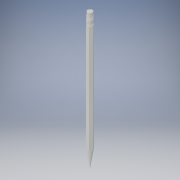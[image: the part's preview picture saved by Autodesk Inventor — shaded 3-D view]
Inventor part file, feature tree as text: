
AUTODESK INVENTOR PART (.ipt)
format: ipt  version: 2017 (Build 210142000, 142)  size: 200,192 bytes
history: native  units: in
note: dims shown in document units (in); Inventor stores cm internally (conversion verified against a paired STEP export)
features: sketch x5, other x4, extrude x2, revolve x1
ambient origin geometry x8: Origin, YZ Plane, XZ Plane, XY Plane, X Axis, Y Axis, Z Axis, Center Point
bodies: Body1 (feature_tree), Body2 (feature_tree)
feature tree (12):
  other  "pencil"
  extrude  "wooden part of pencil"  Depth=0.5578in TaperAngle=0.0deg
  extrude  "pencil graphite"  Depth=0.0047in
  other  "connection for pencil and eraser"
  other  "eraser"
  revolve  "Revolution4"  [1 undecoded]
  sketch  "Sketch1"  dims[d0=0.023in d1=0.5578in d2=0.0in]
  sketch  "Sketch3"  dims[d3=0.0122in d4=0.0047in]
  sketch  "Sketch4"  dims[d10=0.0019in d13=0.0027in]
  sketch  "Sketch5"  dims[d14=0.0167in]
  other  "graphite"
  sketch  "Sketch6"  dims[d15=0.0045in d16=0.0019in d17=0.0028in d18=0.0014in d20=0.0013in d21=0.0005in d22=0.0027in d23=0.0027in d24=0.0027in d25=0.0027in d26=0.0027in d27=0.0019in d28=0.0018in d29=0.0019in d30=90.0deg d31=0.011in d32=0.0154in d33=90.0deg d34=0.006in d35=0.006in d36=1.0in d37=0.0in d39=0.1237in d41=90.0deg]
note: 1 required parameter value undecoded (feature->parameter linkage not recoverable at this tier; creation-order binding heuristic only, values carry confidence <= 0.55)
